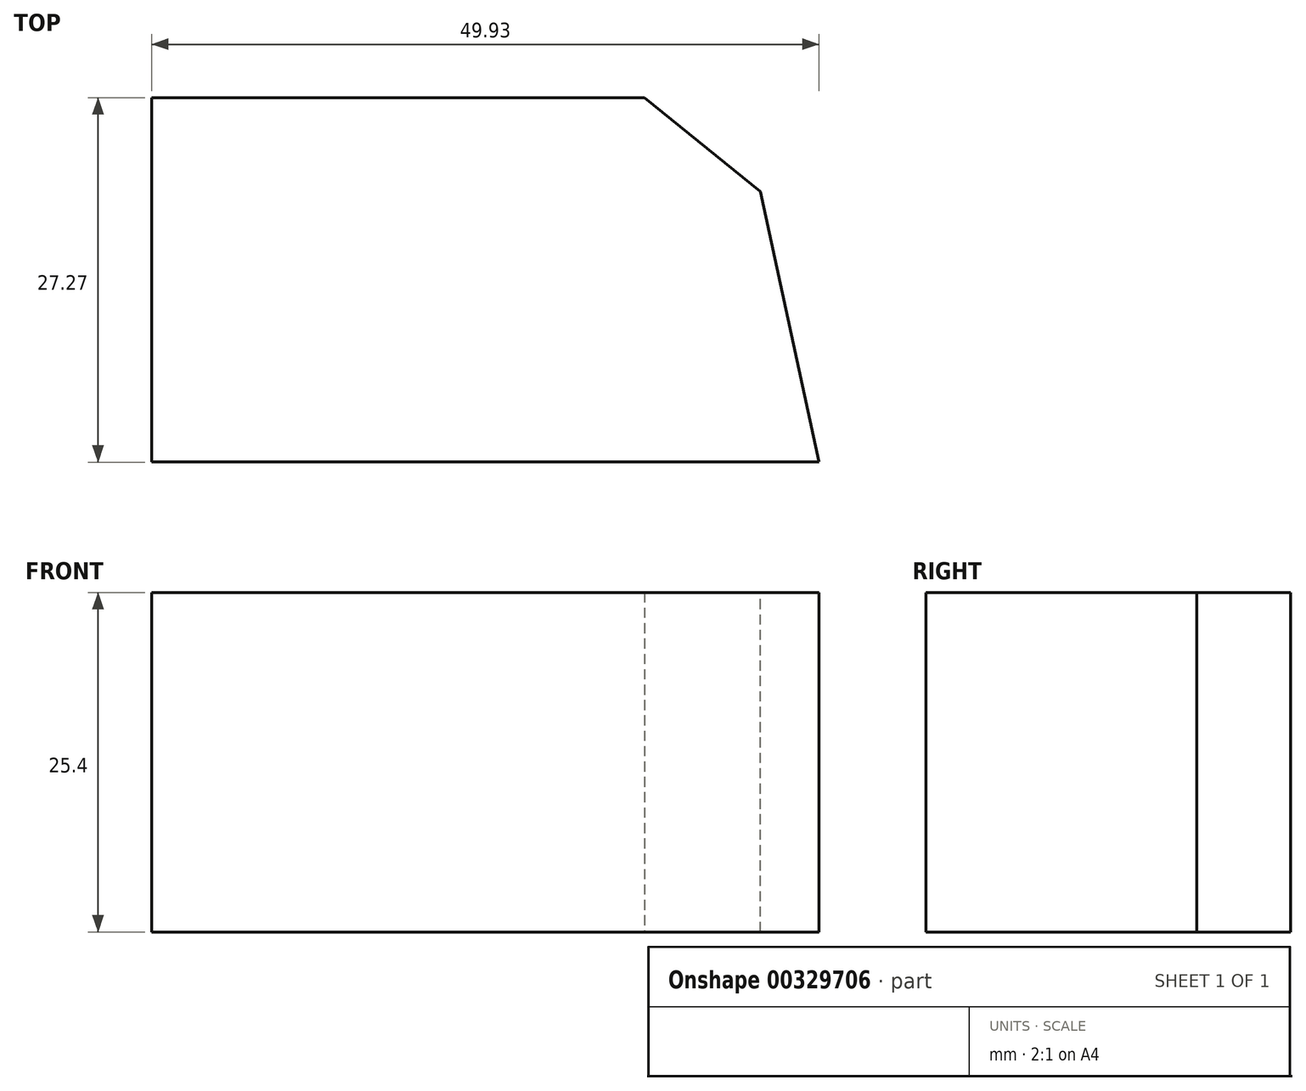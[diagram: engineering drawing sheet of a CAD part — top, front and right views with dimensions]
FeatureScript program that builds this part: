
annotation { "Feature Type Name" : "Feature", "Feature Type Description" : "" }
export const myFeature = defineFeature(function(context is Context, id is Id, definition is map)
    precondition{}
    {
        {
            var Q0;
            Q0=qCreatedBy(makeId("Top.planeOp"),FACE);
            var sketch = newSketch(context, id + "F0", { "sketchPlane" : qUnion([Q0])});
            skLineSegment(sketch, "E0.bottom", {"start": v(0, 0) * mm, "end": v(44.04, 0) * mm});
            skLineSegment(sketch, "E0.top", {"start": v(0, -27.27) * mm, "end": v(49.93, -27.27) * mm});
            skLineSegment(sketch, "E0.left", {"start": v(0, 0) * mm, "end": v(0, -27.27) * mm});
            skLineSegment(sketch, "E0.right", {"start": v(44.04, 0) * mm, "end": v(49.93, -27.27) * mm});
            skSolve(sketch);
        }
        {
            var Q0;
            Q0 = qSketchRegion(id + "F0", true);
            extrude(context, id + "F1", {"entities" : qUnion([Q0]), "depth" : 25.4 * mm});
        }
        {
            var Q0;
            Q0=makeQuery(id+"F1.opExtrude","SWEPT_EDGE",EDGE,{"disambiguationData":[OSD([sQuery(id+"F0.wireOp",EDGE,"E0.bottom"),sQuery(id+"F0.wireOp",EDGE,"E0.right")])]});
            chamfer(context, id + "F2", {"entities" : qUnion([Q0]), "width" : 8.9 * mm, "tangentPropagation" : true});
        }
    });
